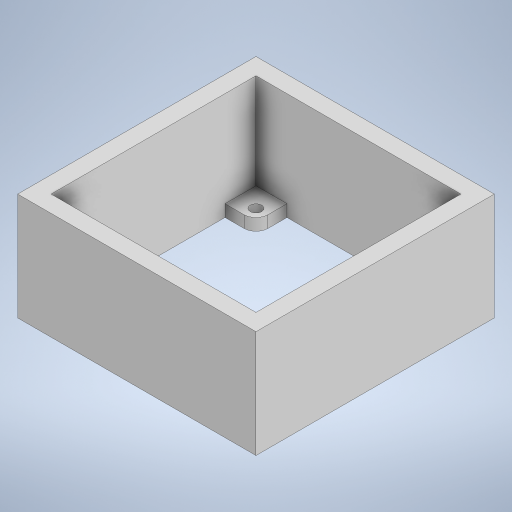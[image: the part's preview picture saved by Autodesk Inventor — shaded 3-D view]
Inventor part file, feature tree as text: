
AUTODESK INVENTOR PART (.ipt)
format: ipt  version: 2024 (Build 280153000, 153)  size: 306,176 bytes
history: native  units: mm
features: extrude x6, sketch x6, projected_geometry x6, shell x1, fillet x1
ambient origin geometry x8: Origin, YZ Plane, XZ Plane, XY Plane, X Axis, Y Axis, Z Axis, Center Point
bodies: Solid1 (feature_tree)
feature tree (20):
  extrude  "Extrusion1"  Depth=86.0mm
  shell  "Shell1"  Thickness=92.0mm
  extrude  "Extrusion2"  Depth=45.0mm
  extrude  "Extrusion3"  Depth=13.0mm
  fillet  "Fillet1"  Radius=13.0mm
  extrude  "Extrusion4"  Depth=40.0mm TaperAngle=0.0deg
  extrude  "Extrusion5"  Depth=4.8mm
  extrude  "Extrusion6"  Depth=10.0mm
  sketch  "Sketch1"  dims[d0=86.0mm d1=86.0mm d2=92.0mm]
  sketch  "Sketch3"  dims[d3=45.0mm d4=0.0mm d5=3.0mm]
  sketch  "Sketch4"  dims[d6=13.0mm d7=13.0mm d8=13.0mm]
  projected_geometry  "Projected Loop1"
  sketch  "Sketch5"  dims[d9=13.0mm d10=40.0mm d11=0.0mm]
  projected_geometry  "Projected Loop2"
  sketch  "Sketch6"  dims[d12=69.6mm d13=4.8mm]
  sketch  "Sketch7"  dims[d14=4.8mm d15=4.8mm d16=4.8mm d17=25.0mm d18=0.0mm d19=5.0mm d20=4.0mm d21=0.0mm d22=4.0mm d23=4.0mm d24=10.0mm d25=0.0mm d26=4.0mm d27=2.0mm d28=0.0mm]
  projected_geometry  "Projected Loop3"
  projected_geometry  "Projected Loop4"
  projected_geometry  "Projected Loop5"
  projected_geometry  "Projected Loop6"
